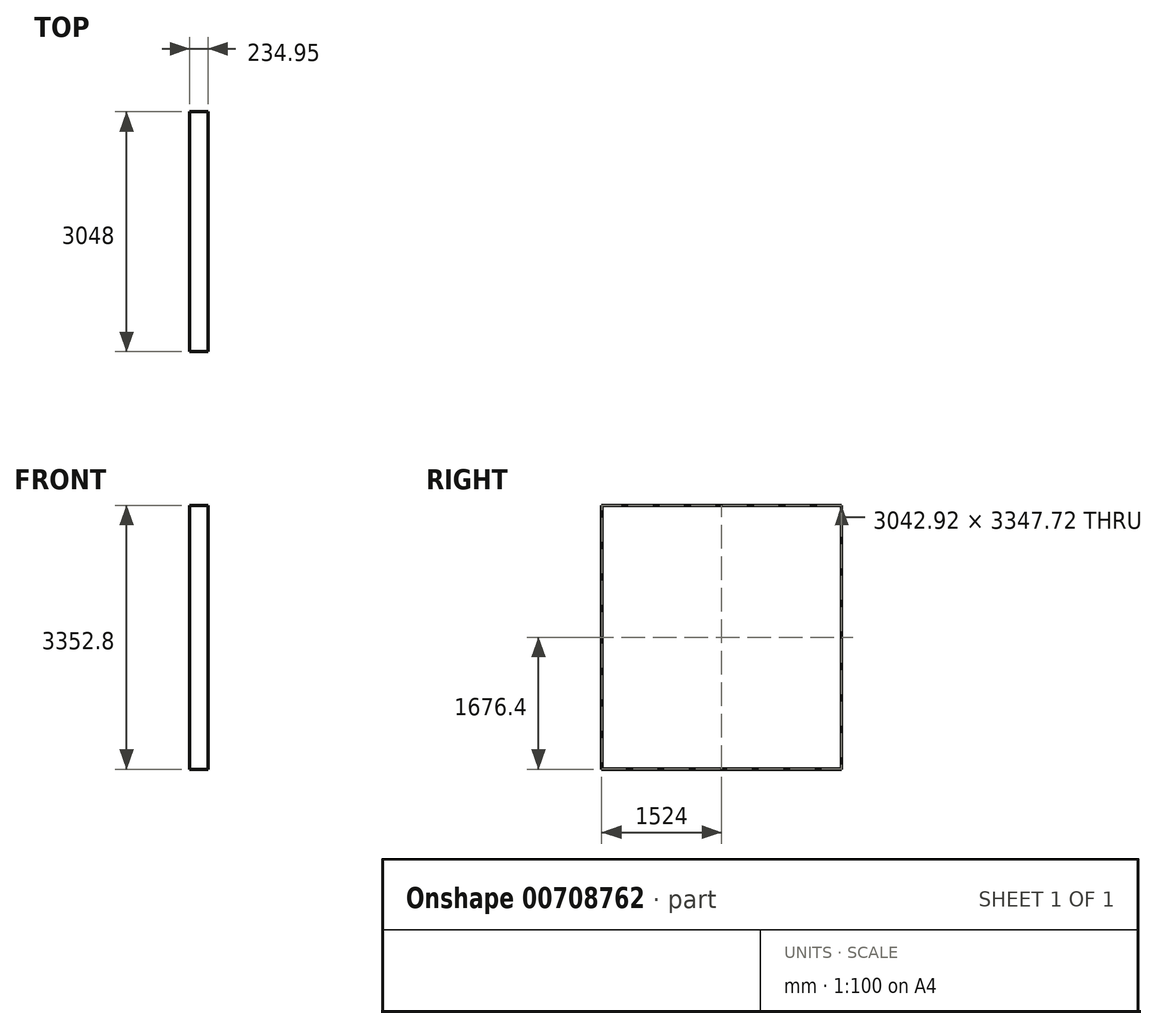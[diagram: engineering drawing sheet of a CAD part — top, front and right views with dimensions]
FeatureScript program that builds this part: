
annotation { "Feature Type Name" : "Feature", "Feature Type Description" : "" }
export const myFeature = defineFeature(function(context is Context, id is Id, definition is map)
    precondition{}
    {
        {
            var Q0;
            Q0=qCreatedBy(makeId("Front.planeOp"),FACE);
            var sketch = newSketch(context, id + "F0", { "sketchPlane" : qUnion([Q0])});
            skLineSegment(sketch, "E0", {"start": v(0, 0) * mm, "end": v(0, 3352.8) * mm});
            skLineSegment(sketch, "E1", {"start": v(0, 3352.8) * mm, "end": v(234.95, 3352.8) * mm});
            skLineSegment(sketch, "E2", {"start": v(234.95, 3352.8) * mm, "end": v(234.95, 0) * mm});
            skLineSegment(sketch, "E3", {"start": v(234.95, 0) * mm, "end": v(0, 0) * mm});
            skSolve(sketch);
        }
        {
            var Q0;
            Q0 = qSketchRegion(id + "F0", true);
            extrude(context, id + "F1", {"entities" : qUnion([Q0]), "depth" : 3048 * mm, "offsetDistance" : 25.4 * mm});
        }
        {
            var Q0;
            Q0=makeQuery(id+"F1.opExtrude","SWEPT_FACE",FACE,{"disambiguationData":[OSD([sQuery(id+"F0.wireOp",EDGE,"E2")])]});
            var sketch = newSketch(context, id + "F2", { "sketchPlane" : qUnion([Q0])});
            skLineSegment(sketch, "E4.bottom", {"start": v(-3045.46, 2.54) * mm, "end": v(-2.54, 2.54) * mm});
            skLineSegment(sketch, "E4.top", {"start": v(-3045.46, 3350.26) * mm, "end": v(-2.54, 3350.26) * mm});
            skLineSegment(sketch, "E4.left", {"start": v(-3045.46, 2.54) * mm, "end": v(-3045.46, 3350.26) * mm});
            skLineSegment(sketch, "E4.right", {"start": v(-2.54, 2.54) * mm, "end": v(-2.54, 3350.26) * mm});
            skSolve(sketch);
        }
        {
            var Q0;
            Q0 = qSketchRegion(id + "F2", true);
            extrude(context, id + "F3", {"entities" : qUnion([Q0]), "operationType" : NewBodyOperationType.REMOVE, "endBound" : BoundingType.UP_TO_NEXT, "oppositeDirection" : true, "depth" : 25.4 * mm, "offsetDistance" : 25.4 * mm});
        }
    });
